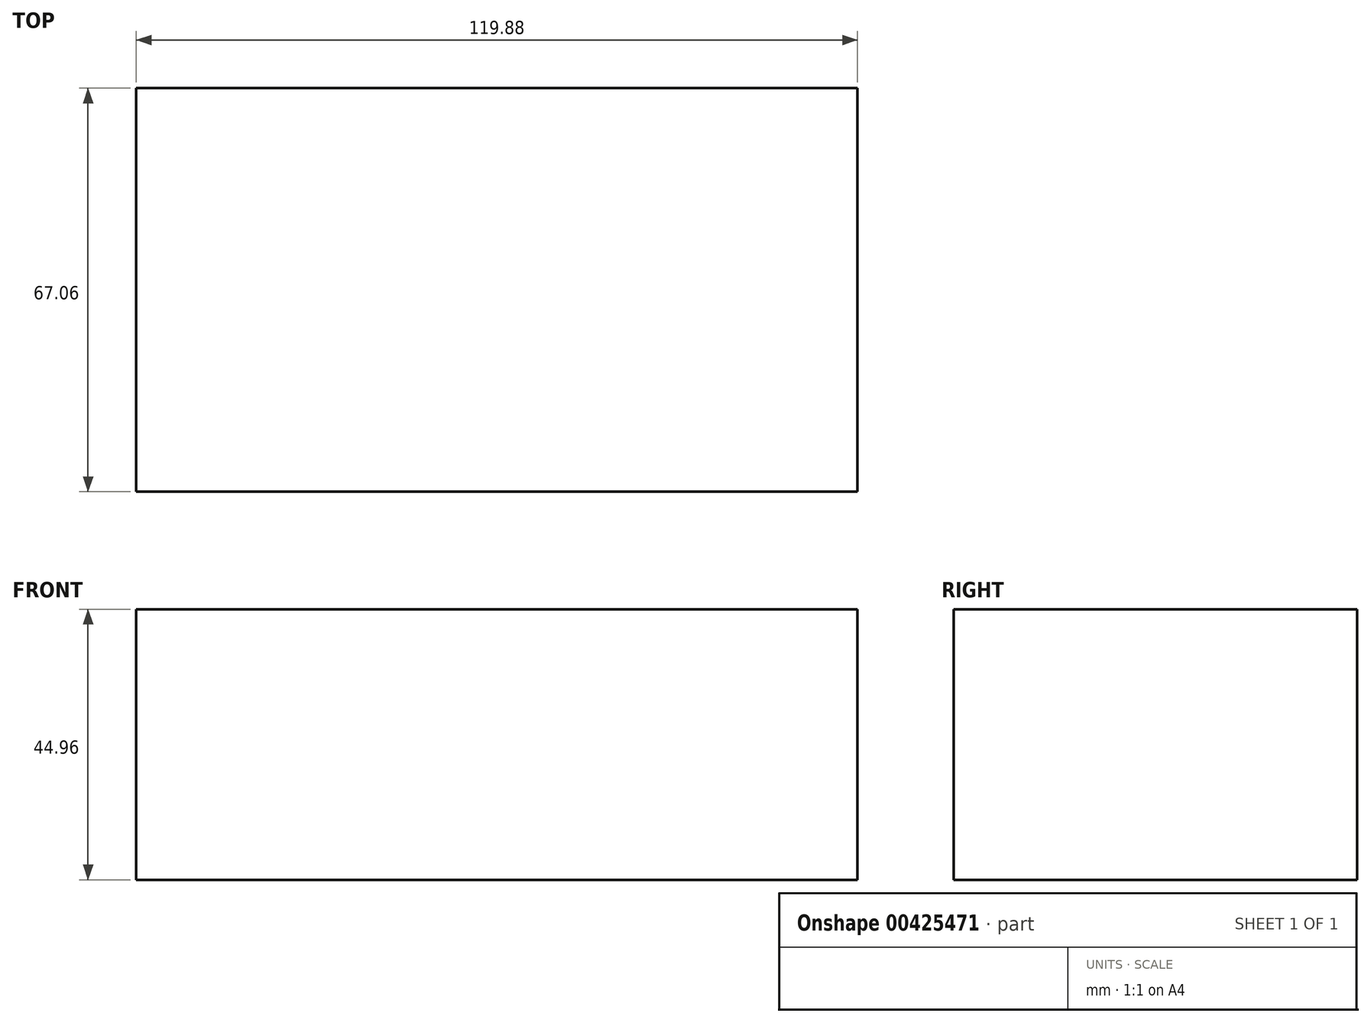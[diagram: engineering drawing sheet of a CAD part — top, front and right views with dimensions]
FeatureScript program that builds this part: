
annotation { "Feature Type Name" : "Feature", "Feature Type Description" : "" }
export const myFeature = defineFeature(function(context is Context, id is Id, definition is map)
    precondition{}
    {
        {
            var Q0;
            Q0=qCreatedBy(makeId("Top.planeOp"),FACE);
            var sketch = newSketch(context, id + "F0", { "sketchPlane" : qUnion([Q0])});
            skLineSegment(sketch, "E0.bottom", {"start": v(59.94, 33.53) * mm, "end": v(-59.94, 33.53) * mm});
            skLineSegment(sketch, "E0.top", {"start": v(59.94, -33.53) * mm, "end": v(-59.94, -33.53) * mm});
            skLineSegment(sketch, "E0.left", {"start": v(59.94, 33.53) * mm, "end": v(59.94, -33.53) * mm});
            skLineSegment(sketch, "E0.right", {"start": v(-59.94, 33.53) * mm, "end": v(-59.94, -33.53) * mm});
            skPoint(sketch, "E0.middle", {"position": v(0, 0) * mm});
            skSolve(sketch);
        }
        {
            var Q0;
            Q0=makeQuery(id+"F0.imprint","IMPRINT",FACE,{"disambiguationData":[TD([[makeQuery(id+"F0.imprint","IMPRINT",EDGE,{"derivedFrom":sQuery(id+"F0.wireOp",EDGE,"E0.bottom")}),1.0]])]});
            extrude(context, id + "F1", {"entities" : qUnion([Q0]), "depth" : 44.96 * mm});
        }
    });
